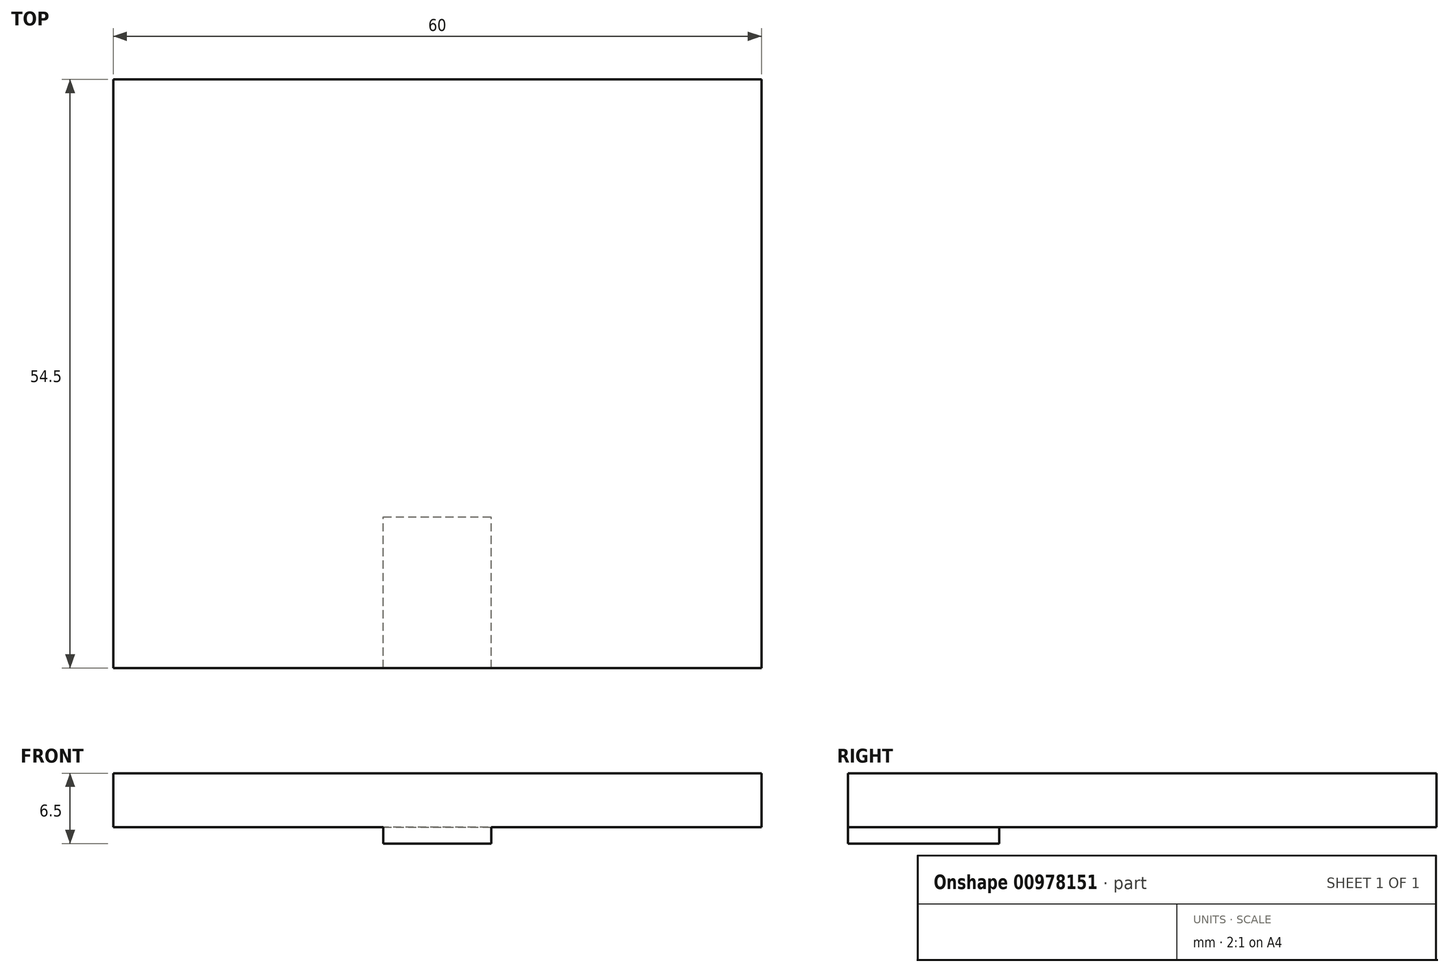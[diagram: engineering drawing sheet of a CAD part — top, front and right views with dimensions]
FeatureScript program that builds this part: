
annotation { "Feature Type Name" : "Feature", "Feature Type Description" : "" }
export const myFeature = defineFeature(function(context is Context, id is Id, definition is map)
    precondition{}
    {
        {
            var Q0;
            Q0=qCreatedBy(makeId("Top.planeOp"),FACE);
            var sketch = newSketch(context, id + "F0", { "sketchPlane" : qUnion([Q0])});
            skLineSegment(sketch, "E0.bottom", {"start": v(30, -27.25) * mm, "end": v(-30, -27.25) * mm});
            skLineSegment(sketch, "E0.top", {"start": v(30, 27.25) * mm, "end": v(-30, 27.25) * mm});
            skLineSegment(sketch, "E0.left", {"start": v(30, -27.25) * mm, "end": v(30, 27.25) * mm});
            skLineSegment(sketch, "E0.right", {"start": v(-30, -27.25) * mm, "end": v(-30, 27.25) * mm});
            skPoint(sketch, "E0.middle", {"position": v(0, 0) * mm});
            skSolve(sketch);
        }
        {
            var Q0;
            Q0 = qSketchRegion(id + "F0", true);
            extrude(context, id + "F1", {"entities" : qUnion([Q0]), "depth" : 5 * mm, "offsetDistance" : 25 * mm});
        }
        {
            var Q0;
            Q0=makeQuery(id+"F1.opExtrude","CAP_FACE",FACE,{"disambiguationData":[OSD([sQuery(id+"F0.wireOp",EDGE,"E0.bottom"),sQuery(id+"F0.wireOp",EDGE,"E0.top"),sQuery(id+"F0.wireOp",EDGE,"E0.left"),sQuery(id+"F0.wireOp",EDGE,"E0.right")])],"isStart":true});
            var sketch = newSketch(context, id + "F2", { "sketchPlane" : qUnion([Q0])});
            skLineSegment(sketch, "E1.bottom", {"start": v(-5, 27.25) * mm, "end": v(5, 27.25) * mm});
            skLineSegment(sketch, "E1.top", {"start": v(-5, 13.25) * mm, "end": v(5, 13.25) * mm});
            skLineSegment(sketch, "E1.left", {"start": v(-5, 27.25) * mm, "end": v(-5, 13.25) * mm});
            skLineSegment(sketch, "E1.right", {"start": v(5, 27.25) * mm, "end": v(5, 13.25) * mm});
            skPoint(sketch, "E1.middle", {"position": v(0, 20.25) * mm});
            skPoint(sketch, "E1.middle.positionSnap0", {"position": v(0, 27.25) * mm});
            skPoint(sketch, "E1.centerSnap0", {"position": v(0, 27.25) * mm});
            skSolve(sketch);
        }
        {
            var Q0;
            Q0 = qSketchRegion(id + "F2", true);
            extrude(context, id + "F3", {"entities" : qUnion([Q0]), "operationType" : NewBodyOperationType.ADD, "depth" : 1.5 * mm, "offsetDistance" : 25 * mm});
        }
    });
